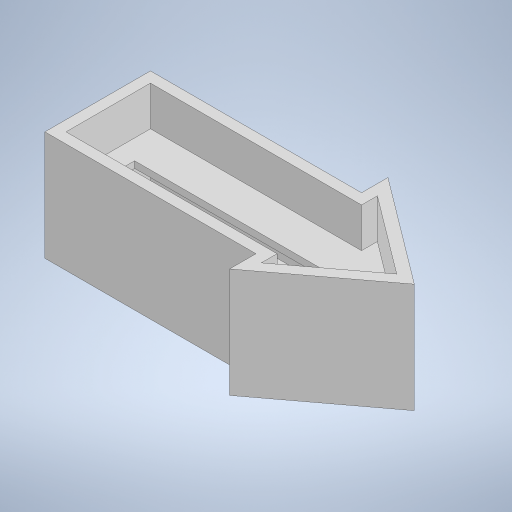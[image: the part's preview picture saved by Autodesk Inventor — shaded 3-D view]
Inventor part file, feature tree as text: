
AUTODESK INVENTOR PART (.ipt)
format: ipt  version: 2023 (Build 270158000, 158)  size: 286,720 bytes
history: native  units: in
note: dims shown in document units (in); Inventor stores cm internally (conversion verified against a paired STEP export)
features: sketch x8, other x3, extrude x3, projected_geometry x2
ambient origin geometry x8: Origin, YZ Plane, XZ Plane, XY Plane, X Axis, Y Axis, Z Axis, Center Point
bodies: Solid1 (feature_tree)
feature tree (16):
  other  "Part_5_ledholder.ipt"
  extrude  "Extrusion1"  Depth=1.0in TaperAngle=0.0deg
  extrude  "Extrusion2"  Depth=0.1in
  extrude  "Extrusion3"  Depth=0.75in TaperAngle=0.0deg
  other  "Solid1::Part_5_ledholder.ipt"
  other  "TaggingFeature1"
  sketch  "Sketch1"  dims[d0=0.3937in d1=1.0in d2=0.0in]
  sketch  "Sketch2"  dims[d3=0.6in d4=0.0in d5=0.1in]
  sketch  "Sketch3"  dims[d6=0.0in d7=0.75in d8=0.0in]
  sketch  "Sketch4"
  sketch  "Sketch6"
  sketch  "Sketch7"
  projected_geometry  "Projected Loop1"
  sketch  "Sketch8"
  projected_geometry  "Projected Loop2"
  sketch  "Sketch9"
